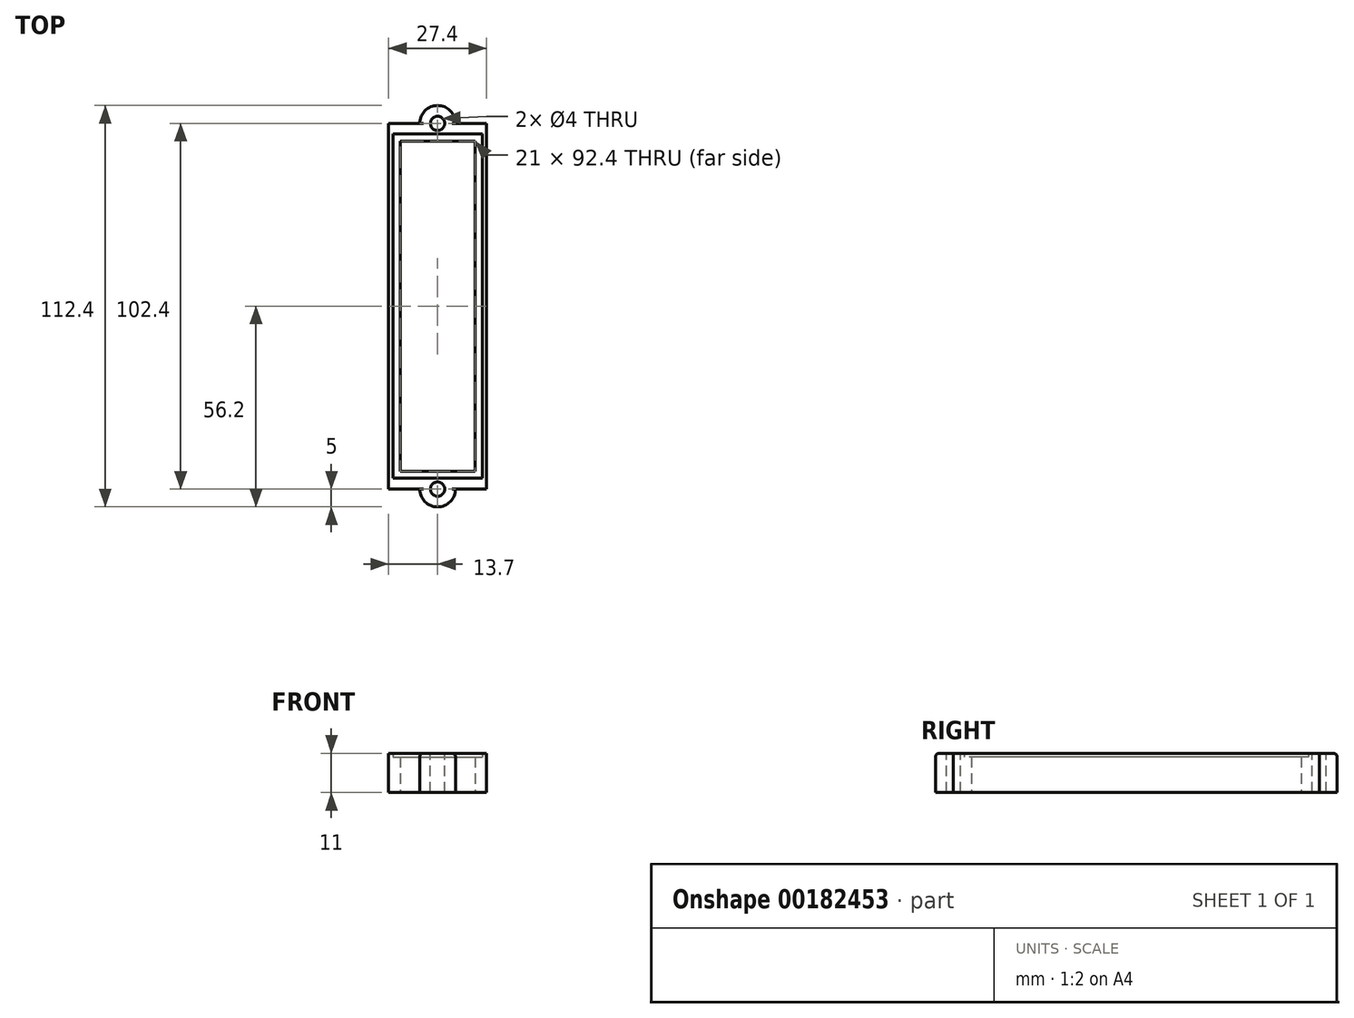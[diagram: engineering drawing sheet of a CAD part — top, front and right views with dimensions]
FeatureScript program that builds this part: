
annotation { "Feature Type Name" : "Feature", "Feature Type Description" : "" }
export const myFeature = defineFeature(function(context is Context, id is Id, definition is map)
    precondition{}
    {
        {
            var Q0;
            Q0=qCreatedBy(makeId("Top.planeOp"),FACE);
            var sketch = newSketch(context, id + "F0", { "sketchPlane" : qUnion([Q0])});
            skLineSegment(sketch, "E0.bottom", {"start": v(-12.5, 48.2) * mm, "end": v(12.5, 48.2) * mm});
            skLineSegment(sketch, "E0.top", {"start": v(-12.5, -48.2) * mm, "end": v(12.5, -48.2) * mm});
            skLineSegment(sketch, "E0.left", {"start": v(-12.5, 48.2) * mm, "end": v(-12.5, -48.2) * mm});
            skLineSegment(sketch, "E0.right", {"start": v(12.5, 48.2) * mm, "end": v(12.5, -48.2) * mm});
            skPoint(sketch, "E0.middle", {"position": v(0, 0) * mm});
            skLineSegment(sketch, "E1.bottom", {"start": v(-10.5, 46.2) * mm, "end": v(10.5, 46.2) * mm});
            skLineSegment(sketch, "E1.top", {"start": v(-10.5, -46.2) * mm, "end": v(10.5, -46.2) * mm});
            skLineSegment(sketch, "E1.left", {"start": v(-10.5, 46.2) * mm, "end": v(-10.5, -46.2) * mm});
            skLineSegment(sketch, "E1.right", {"start": v(10.5, 46.2) * mm, "end": v(10.5, -46.2) * mm});
            skLineSegment(sketch, "E2.bottom", {"start": v(-13.7, 51.2) * mm, "end": v(13.7, 51.2) * mm});
            skLineSegment(sketch, "E2.top", {"start": v(-13.7, -51.2) * mm, "end": v(13.7, -51.2) * mm});
            skLineSegment(sketch, "E2.left", {"start": v(-13.7, 51.2) * mm, "end": v(-13.7, -51.2) * mm});
            skLineSegment(sketch, "E2.right", {"start": v(13.7, 51.2) * mm, "end": v(13.7, -51.2) * mm});
            skLineSegment(sketch, "E3", {"start": v(0, -56.2) * mm, "end": v(0, 56.2) * mm, "construction": true});
            skPoint(sketch, "E4", {"position": v(0, 51.2) * mm});
            skPoint(sketch, "E5", {"position": v(0, -48.2) * mm});
            skArc(sketch, "E6", {"start": v(-5, -51.2) * mm, "mid": v(0, -56.2) * mm, "end": v(5, -51.2) * mm});
            skArc(sketch, "E7", {"start": v(5, 51.2) * mm, "mid": v(0, 56.2) * mm, "end": v(-5, 51.2) * mm});
            skSolve(sketch);
        }
        {
            var Q0;
            Q0=makeQuery(id+"F0.imprint","IMPRINT",FACE,{"disambiguationData":[TD([[makeQuery(id+"F0.imprint","IMPRINT",EDGE,{"derivedFrom":sQuery(id+"F0.wireOp",EDGE,"E0.bottom")}),-1.0]])]});
            extrude(context, id + "F1", {"entities" : qUnion([Q0]), "depth" : 10 * mm, "offsetDistance" : 25 * mm});
        }
        {
            var Q0;
            Q0=makeQuery(id+"F0.imprint","IMPRINT",FACE,{"disambiguationData":[TD([[makeQuery(id+"F0.imprint","IMPRINT",EDGE,{"derivedFrom":sQuery(id+"F0.wireOp",EDGE,"E0.bottom")}),1.0]])]});
            var Q1;
            {var subQ0=sQuery(id+"F0.wireOp",EDGE,"E6");Q1=makeQuery(id+"F0.imprint","IMPRINT",FACE,{"disambiguationData":[TD([[makeQuery(id+"F0.imprint","IMPRINT",EDGE,{"derivedFrom":subQ0}),1.0]])]});}
            var Q2;
            {var subQ0=sQuery(id+"F0.wireOp",EDGE,"E7");Q2=makeQuery(id+"F0.imprint","IMPRINT",FACE,{"disambiguationData":[TD([[makeQuery(id+"F0.imprint","IMPRINT",EDGE,{"derivedFrom":subQ0}),1.0]])]});}
            extrude(context, id + "F2", {"entities" : qUnion([Q0, Q1, Q2]), "operationType" : NewBodyOperationType.ADD, "depth" : 11 * mm, "offsetDistance" : 25 * mm});
        }
        {
            var Q0;
            Q0=sQuery(id+"F0.wireOp",VERTEX,"E4");
            var Q1;
            Q1=sQuery(id+"F0.wireOp",VERTEX,"E6.center");
            var Q2;
            Q2=makeQuery(id+"F1.opExtrude","SWEPT_BODY",BODY,{"disambiguationData":[OSD([sQuery(id+"F0.wireOp",EDGE,"E0.bottom"),sQuery(id+"F0.wireOp",EDGE,"E0.top"),sQuery(id+"F0.wireOp",EDGE,"E0.left"),sQuery(id+"F0.wireOp",EDGE,"E0.right"),sQuery(id+"F0.wireOp",EDGE,"E1.bottom"),sQuery(id+"F0.wireOp",EDGE,"E1.top"),sQuery(id+"F0.wireOp",EDGE,"E1.left"),sQuery(id+"F0.wireOp",EDGE,"E1.right")])]});
            hole(context, id + "F3", {"style" : HoleStyle.SIMPLE, "endStyle" : HoleEndStyle.BLIND, "oppositeDirection" : true, "holeDiameter" : 4 * mm, "majorDiameter" : 5 * mm, "holeDepth" : 15 * mm, "tappedDepth" : 12 * mm, "tapClearance" : 3, "locations" : qUnion([Q0, Q1]), "scope" : qUnion([Q2])});
        }
        {
            var Q0;
            Q0=makeQuery(id+"F2.opExtrude","CAP_EDGE",EDGE,{"disambiguationData":[OSD([sQuery(id+"F0.wireOp",EDGE,"E7")])],"isStart":false});
            var Q1;
            Q1=makeQuery(id+"F2.opExtrude","CAP_EDGE",EDGE,{"disambiguationData":[OSD([sQuery(id+"F0.wireOp",EDGE,"E6")])],"isStart":false});
            fillet(context, id + "F4", {"entities" : qUnion([Q0, Q1]), "tangentPropagation" : true, "radius" : 1 * mm, "defaultsChanged" : false, "vertexSettings" : [], "allowEdgeOverflow" : false});
        }
    });
